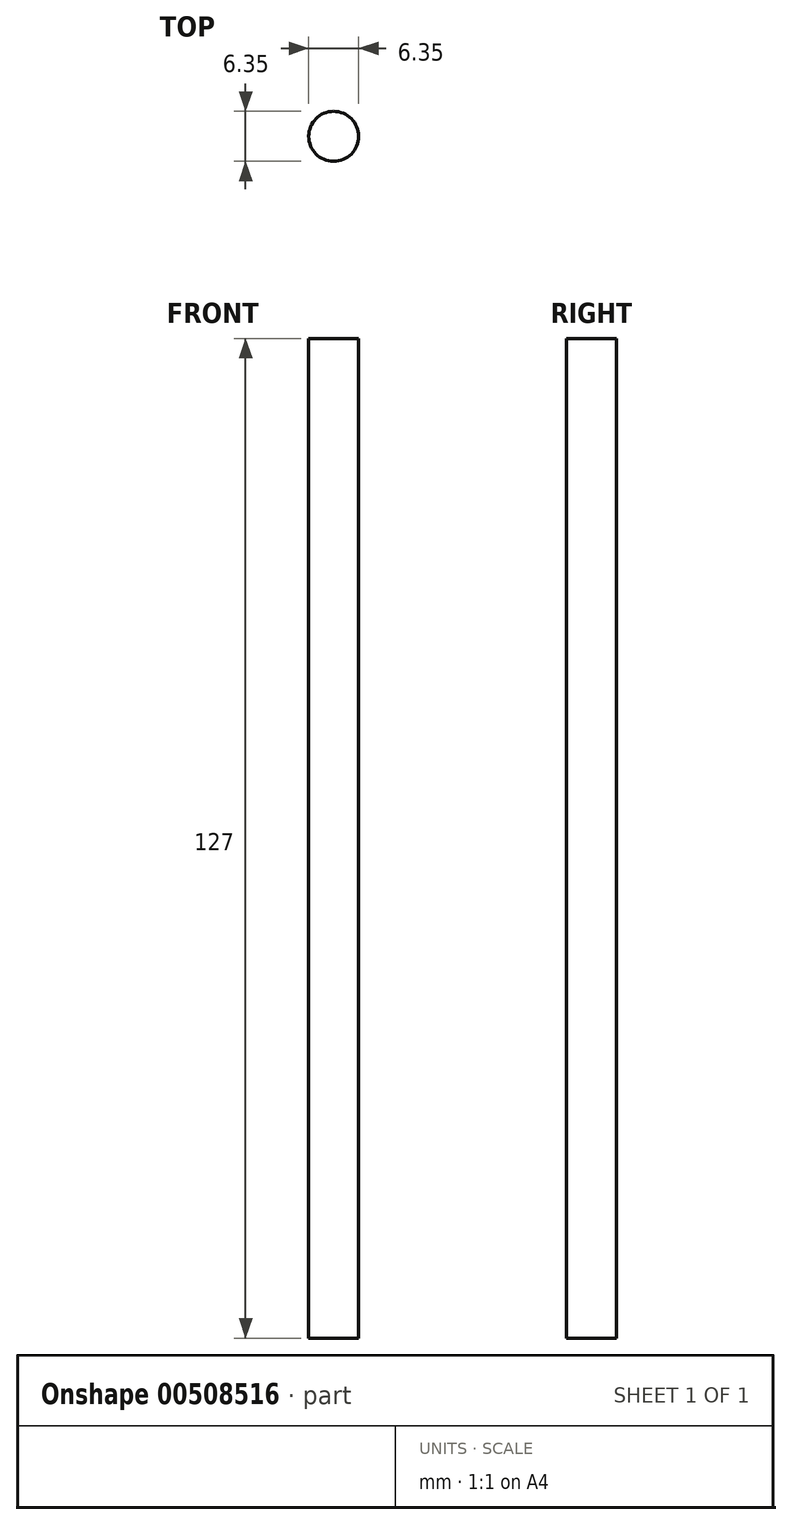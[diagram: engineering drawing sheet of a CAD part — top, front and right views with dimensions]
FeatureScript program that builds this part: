
annotation { "Feature Type Name" : "Feature", "Feature Type Description" : "" }
export const myFeature = defineFeature(function(context is Context, id is Id, definition is map)
    precondition{}
    {
        {
            var Q0;
            Q0=qCreatedBy(makeId("Top.planeOp"),FACE);
            var sketch = newSketch(context, id + "F0", { "sketchPlane" : qUnion([Q0])});
            skCircle(sketch, "E0", {"center": v(3.18, -3.18) * mm, "radius": 3.18 * mm});
            skSolve(sketch);
        }
        {
            var Q0;
            Q0=makeQuery(id+"F0.imprint","IMPRINT",FACE,{"disambiguationData":[TD([[makeQuery(id+"F0.imprint","IMPRINT",EDGE,{"derivedFrom":sQuery(id+"F0.wireOp",EDGE,"E0")}),1.0]])]});
            extrude(context, id + "F1", {"entities" : qUnion([Q0]), "depth" : 127 * mm, "offsetDistance" : 25.4 * mm});
        }
    });
